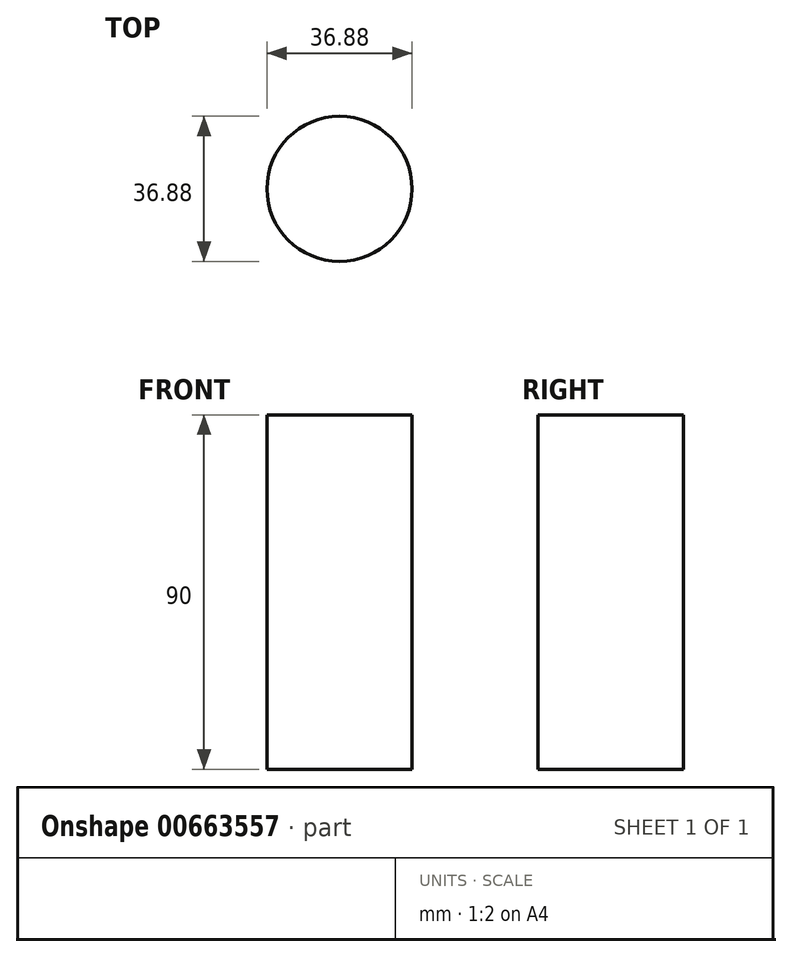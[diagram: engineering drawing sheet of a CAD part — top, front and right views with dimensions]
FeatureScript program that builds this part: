
annotation { "Feature Type Name" : "Feature", "Feature Type Description" : "" }
export const myFeature = defineFeature(function(context is Context, id is Id, definition is map)
    precondition{}
    {
        {
            var Q0;
            Q0=qCreatedBy(makeId("Top.planeOp"),FACE);
            var sketch = newSketch(context, id + "F0", { "sketchPlane" : qUnion([Q0])});
            skCircle(sketch, "E0", {"center": v(0, 0) * mm, "radius": 18.44 * mm});
            skSolve(sketch);
        }
        {
            var Q0;
            Q0 = qSketchRegion(id + "F0", true);
            extrude(context, id + "F1", {"entities" : qUnion([Q0]), "depth" : 90 * mm, "offsetDistance" : 25 * mm});
        }
    });
